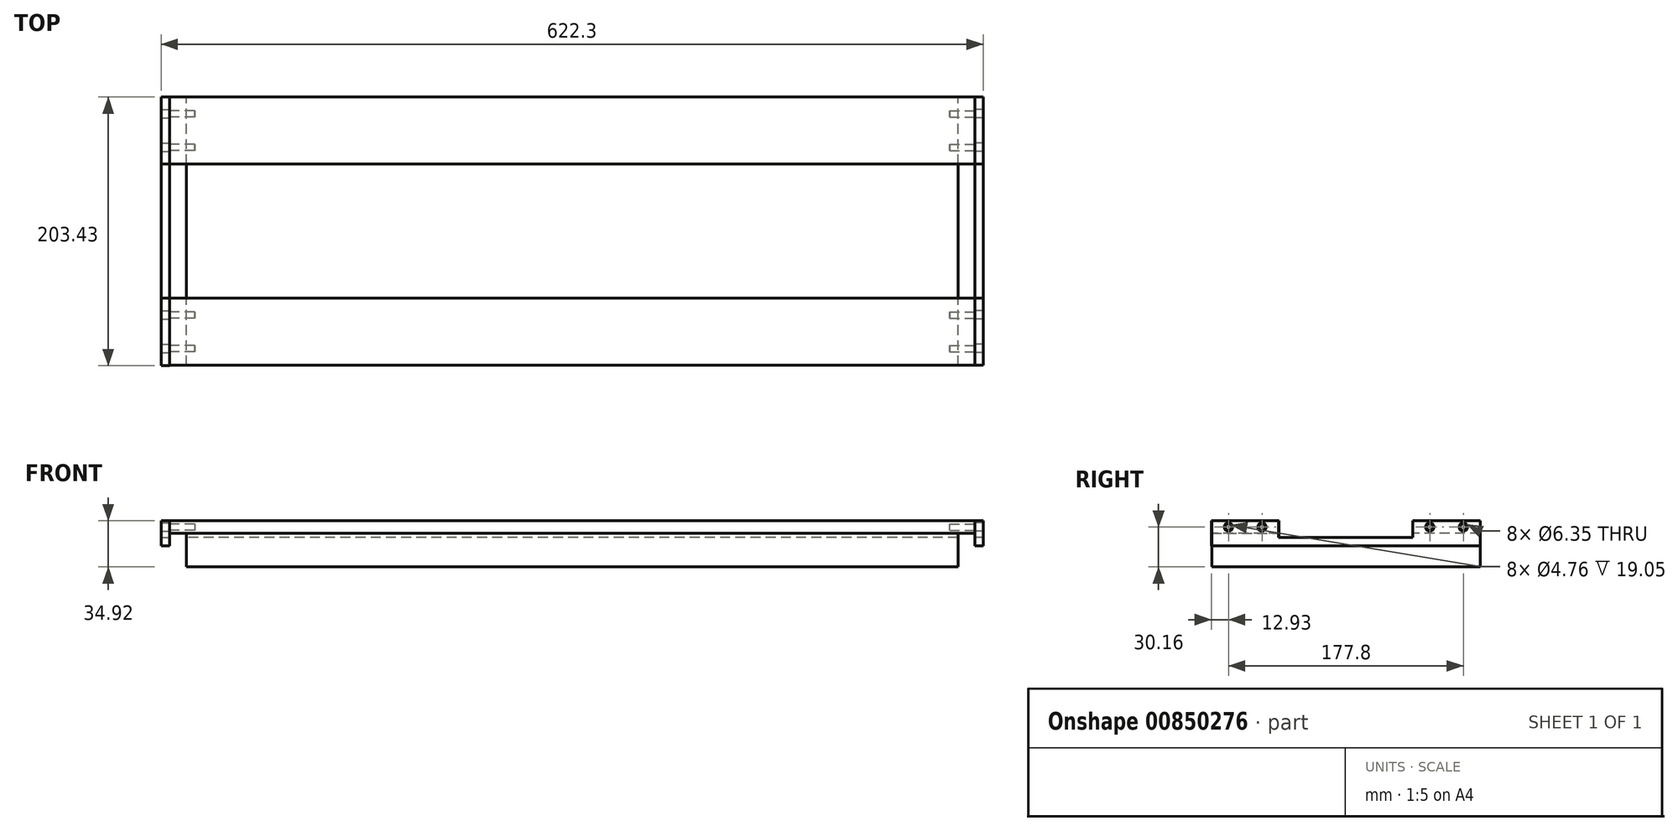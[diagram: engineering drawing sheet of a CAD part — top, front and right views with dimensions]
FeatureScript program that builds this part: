
annotation { "Feature Type Name" : "Feature", "Feature Type Description" : "" }
export const myFeature = defineFeature(function(context is Context, id is Id, definition is map)
    precondition{}
    {
        {
            var Q0;
            Q0=qCreatedBy(makeId("Right.planeOp"),FACE);
            var sketch = newSketch(context, id + "F0", { "sketchPlane" : qUnion([Q0])});
            skLineSegment(sketch, "E0.bottom", {"start": v(-50.8, -4.7) * mm, "end": v(-101.6, -4.7) * mm});
            skLineSegment(sketch, "E0.top", {"start": v(-50.8, 4.7) * mm, "end": v(-101.6, 4.7) * mm});
            skLineSegment(sketch, "E0.left", {"start": v(-50.8, -4.7) * mm, "end": v(-50.8, 4.7) * mm});
            skLineSegment(sketch, "E0.right", {"start": v(-101.6, -4.7) * mm, "end": v(-101.6, 4.7) * mm});
            skPoint(sketch, "E0.middle", {"position": v(-76.2, 0) * mm});
            skLineSegment(sketch, "E1.bottom", {"start": v(101.6, -4.76) * mm, "end": v(50.8, -4.76) * mm});
            skLineSegment(sketch, "E1.top", {"start": v(101.6, 4.76) * mm, "end": v(50.8, 4.76) * mm});
            skLineSegment(sketch, "E1.left", {"start": v(101.6, -4.76) * mm, "end": v(101.6, 4.76) * mm});
            skLineSegment(sketch, "E1.right", {"start": v(50.8, -4.76) * mm, "end": v(50.8, 4.76) * mm});
            skPoint(sketch, "E1.middle", {"position": v(76.2, 0) * mm});
            skSolve(sketch);
        }
        {
            var Q0;
            Q0=makeQuery(id+"F0.imprint","IMPRINT",FACE,{"disambiguationData":[TD([[makeQuery(id+"F0.imprint","IMPRINT",EDGE,{"derivedFrom":sQuery(id+"F0.wireOp",EDGE,"E0.bottom")}),-1.0]])]});
            var Q1;
            Q1=makeQuery(id+"F0.imprint","IMPRINT",FACE,{"disambiguationData":[TD([[makeQuery(id+"F0.imprint","IMPRINT",EDGE,{"derivedFrom":sQuery(id+"F0.wireOp",EDGE,"E1.bottom")}),-1.0]])]});
            extrude(context, id + "F1", {"entities" : qUnion([Q0, Q1]), "endBound" : BoundingType.SYMMETRIC, "depth" : 609.6 * mm, "offsetDistance" : 25.4 * mm});
        }
        {
            var Q0;
            Q0=makeQuery(id+"F1.opExtrude","CAP_FACE",FACE,{"disambiguationData":[OSD([sQuery(id+"F0.wireOp",EDGE,"E0.bottom"),sQuery(id+"F0.wireOp",EDGE,"E0.top"),sQuery(id+"F0.wireOp",EDGE,"E0.left"),sQuery(id+"F0.wireOp",EDGE,"E0.right")])],"isStart":false});
            var sketch = newSketch(context, id + "F2", { "sketchPlane" : qUnion([Q0])});
            skLineSegment(sketch, "E2", {"start": v(-101.6, 0) * mm, "end": v(-50.8, 0) * mm, "construction": true});
            skCircle(sketch, "E3", {"center": v(-88.9, 0) * mm, "radius": 2.38 * mm});
            skCircle(sketch, "E4", {"center": v(-63.5, 0) * mm, "radius": 2.38 * mm});
            skLineSegment(sketch, "E5", {"start": v(-50.8, 0) * mm, "end": v(103.45, 0) * mm, "construction": true});
            skCircle(sketch, "E6", {"center": v(63.5, 0) * mm, "radius": 2.38 * mm});
            skCircle(sketch, "E7", {"center": v(88.9, 0) * mm, "radius": 2.38 * mm});
            skSolve(sketch);
        }
        {
            var Q0;
            Q0 = qSketchRegion(id + "F2", true);
            extrude(context, id + "F3", {"entities" : qUnion([Q0]), "operationType" : NewBodyOperationType.REMOVE, "oppositeDirection" : true, "depth" : 19.05 * mm, "offsetDistance" : 25.4 * mm});
        }
        {
            var Q0;
            Q0=makeQuery(id+"F1.opExtrude","CAP_FACE",FACE,{"disambiguationData":[OSD([sQuery(id+"F0.wireOp",EDGE,"E1.bottom"),sQuery(id+"F0.wireOp",EDGE,"E1.top"),sQuery(id+"F0.wireOp",EDGE,"E1.left"),sQuery(id+"F0.wireOp",EDGE,"E1.right")])],"isStart":true});
            var sketch = newSketch(context, id + "F4", { "sketchPlane" : qUnion([Q0])});
            skLineSegment(sketch, "E8", {"start": v(-101.6, 0) * mm, "end": v(107.91, 0) * mm, "construction": true});
            skCircle(sketch, "E9", {"center": v(-88.9, 0) * mm, "radius": 2.38 * mm});
            skCircle(sketch, "E10", {"center": v(-63.5, 0) * mm, "radius": 2.38 * mm});
            skCircle(sketch, "E11", {"center": v(63.5, 0) * mm, "radius": 2.38 * mm});
            skCircle(sketch, "E12", {"center": v(88.9, 0) * mm, "radius": 2.38 * mm});
            skSolve(sketch);
        }
        {
            var Q0;
            Q0 = qSketchRegion(id + "F4", true);
            extrude(context, id + "F5", {"entities" : qUnion([Q0]), "operationType" : NewBodyOperationType.REMOVE, "oppositeDirection" : true, "depth" : 19.05 * mm, "offsetDistance" : 25.4 * mm});
        }
        {
            var Q0;
            Q0=makeQuery(id+"F1.opExtrude","CAP_FACE",FACE,{"disambiguationData":[OSD([sQuery(id+"F0.wireOp",EDGE,"E1.bottom"),sQuery(id+"F0.wireOp",EDGE,"E1.top"),sQuery(id+"F0.wireOp",EDGE,"E1.left"),sQuery(id+"F0.wireOp",EDGE,"E1.right")])],"isStart":true});
            var sketch = newSketch(context, id + "F6", { "sketchPlane" : qUnion([Q0])});
            skLineSegment(sketch, "E13.bottom", {"start": v(-101.6, 4.76) * mm, "end": v(-50.8, 4.76) * mm});
            skLineSegment(sketch, "E13.top", {"start": v(-101.6, -14.29) * mm, "end": v(101.83, -14.29) * mm});
            skLineSegment(sketch, "E13.left", {"start": v(-101.6, 4.76) * mm, "end": v(-101.6, -14.29) * mm});
            skLineSegment(sketch, "E13.right", {"start": v(101.83, 4.76) * mm, "end": v(101.83, -14.29) * mm});
            skLineSegment(sketch, "E14.top", {"start": v(-50.8, -7.94) * mm, "end": v(50.74, -7.94) * mm});
            skLineSegment(sketch, "E14.left", {"start": v(-50.8, 4.76) * mm, "end": v(-50.8, -7.94) * mm});
            skLineSegment(sketch, "E14.right", {"start": v(50.74, 4.76) * mm, "end": v(50.74, -7.94) * mm});
            skLineSegment(sketch, "E15.trimOffspring", {"start": v(50.74, 4.76) * mm, "end": v(101.83, 4.76) * mm});
            skCircle(sketch, "E16", {"center": v(-88.9, 0) * mm, "radius": 3.18 * mm});
            skCircle(sketch, "E17", {"center": v(-63.5, 0) * mm, "radius": 3.18 * mm});
            skCircle(sketch, "E18", {"center": v(63.5, 0) * mm, "radius": 3.18 * mm});
            skCircle(sketch, "E19", {"center": v(88.9, 0) * mm, "radius": 3.18 * mm});
            skSolve(sketch);
        }
        {
            var Q0;
            {var subQ3=sQuery(id+"F6.wireOp",EDGE,"E13.top");Q0=makeQuery(id+"F6.imprint","IMPRINT",FACE,{"disambiguationData":[TD([[makeQuery(id+"F6.imprint","IMPRINT",EDGE,{"derivedFrom":subQ3}),1.0]])]});}
            var Q1;
            {var subQ2=sQuery(id+"F6.wireOp",EDGE,"E13.bottom");Q1=makeQuery(id+"F6.imprint","IMPRINT",FACE,{"disambiguationData":[TD([[makeQuery(id+"F6.imprint","IMPRINT",EDGE,{"derivedFrom":subQ2}),-1.0]])]});}
            extrude(context, id + "F7", {"entities" : qUnion([Q0, Q1]), "depth" : 6.35 * mm, "offsetDistance" : 25.4 * mm});
        }
        {
            var Q0;
            Q0=makeQuery(id+"F1.opExtrude","CAP_FACE",FACE,{"disambiguationData":[OSD([sQuery(id+"F0.wireOp",EDGE,"E0.bottom"),sQuery(id+"F0.wireOp",EDGE,"E0.top"),sQuery(id+"F0.wireOp",EDGE,"E0.left"),sQuery(id+"F0.wireOp",EDGE,"E0.right")])],"isStart":false});
            var sketch = newSketch(context, id + "F8", { "sketchPlane" : qUnion([Q0])});
            skLineSegment(sketch, "E20.bottom", {"start": v(-101.6, 4.7) * mm, "end": v(-50.8, 4.7) * mm});
            skLineSegment(sketch, "E20.top", {"start": v(-101.6, -14.35) * mm, "end": v(101.6, -14.35) * mm});
            skLineSegment(sketch, "E20.left", {"start": v(-101.6, 4.7) * mm, "end": v(-101.6, -14.35) * mm});
            skLineSegment(sketch, "E20.right", {"start": v(101.6, 4.7) * mm, "end": v(101.6, -14.35) * mm});
            skLineSegment(sketch, "E21.top", {"start": v(-50.8, -8) * mm, "end": v(50.8, -8) * mm});
            skLineSegment(sketch, "E21.left", {"start": v(-50.8, 4.7) * mm, "end": v(-50.8, -8) * mm});
            skLineSegment(sketch, "E21.right", {"start": v(50.8, 4.7) * mm, "end": v(50.8, -8) * mm});
            skLineSegment(sketch, "E22.trimOffspring", {"start": v(50.8, 4.7) * mm, "end": v(101.6, 4.7) * mm});
            skCircle(sketch, "E23", {"center": v(-88.9, 0) * mm, "radius": 3.18 * mm});
            skCircle(sketch, "E24", {"center": v(-63.5, 0) * mm, "radius": 3.18 * mm});
            skCircle(sketch, "E25", {"center": v(63.5, 0) * mm, "radius": 3.18 * mm});
            skCircle(sketch, "E26", {"center": v(88.9, 0) * mm, "radius": 3.18 * mm});
            skSolve(sketch);
        }
        {
            var Q0;
            Q0 = qSketchRegion(id + "F8", true);
            extrude(context, id + "F9", {"entities" : qUnion([Q0]), "depth" : 6.35 * mm, "offsetDistance" : 25.4 * mm});
        }
        {
            var Q0;
            Q0=makeQuery(id+"F7.opExtrude","CAP_FACE",FACE,{"disambiguationData":[OSD([sQuery(id+"F6.wireOp",EDGE,"E13.bottom"),sQuery(id+"F6.wireOp",EDGE,"E13.top"),sQuery(id+"F6.wireOp",EDGE,"E13.left"),sQuery(id+"F6.wireOp",EDGE,"E13.right"),sQuery(id+"F6.wireOp",EDGE,"E14.top"),sQuery(id+"F6.wireOp",EDGE,"E14.left"),sQuery(id+"F6.wireOp",EDGE,"E14.right"),sQuery(id+"F6.wireOp",EDGE,"E15.trimOffspring"),sQuery(id+"F6.wireOp",EDGE,"E16"),sQuery(id+"F6.wireOp",EDGE,"E17"),sQuery(id+"F6.wireOp",EDGE,"E18"),sQuery(id+"F6.wireOp",EDGE,"E19")])],"isStart":true});
            cPlane(context, id + "F10", {"entities" : qUnion([Q0]), "cplaneType" : CPlaneType.OFFSET, "offset" : 12.7 * mm, "width" : 152.4 * mm, "height" : 152.4 * mm});
        }
        {
            var Q0;
            Q0=qCreatedBy(id+"F10.planeOp",FACE);
            var sketch = newSketch(context, id + "F11", { "sketchPlane" : qUnion([Q0])});
            skLineSegment(sketch, "E27.bottom", {"start": v(101.6, -30.16) * mm, "end": v(-101.6, -30.16) * mm});
            skLineSegment(sketch, "E27.left", {"start": v(101.6, -30.16) * mm, "end": v(101.6, -4.76) * mm});
            skLineSegment(sketch, "E27.right", {"start": v(-101.6, -30.16) * mm, "end": v(-101.6, -4.76) * mm});
            skPoint(sketch, "E27.middle", {"position": v(0, 0) * mm});
            skLineSegment(sketch, "E28", {"start": v(-101.6, -4.76) * mm, "end": v(-50.8, -4.76) * mm});
            skPoint(sketch, "E29.orphan", {"position": v(-101.6, 30.16) * mm});
            skPoint(sketch, "E30.orphan", {"position": v(101.6, 30.16) * mm});
            skLineSegment(sketch, "E31.top", {"start": v(50.8, -7.94) * mm, "end": v(-50.8, -7.94) * mm});
            skLineSegment(sketch, "E31.left", {"start": v(50.8, -4.76) * mm, "end": v(50.8, -7.94) * mm});
            skLineSegment(sketch, "E31.right", {"start": v(-50.8, -4.76) * mm, "end": v(-50.8, -7.94) * mm});
            skPoint(sketch, "E31.bottom.end.orphan", {"position": v(-50.8, 7.94) * mm});
            skPoint(sketch, "E31.bottom.start.orphan", {"position": v(50.8, 7.94) * mm});
            skLineSegment(sketch, "E32.trimOffspring", {"start": v(50.8, -4.76) * mm, "end": v(101.6, -4.76) * mm});
            skSolve(sketch);
        }
        {
            var Q0;
            Q0 = qSketchRegion(id + "F11", true);
            extrude(context, id + "F12", {"entities" : qUnion([Q0]), "depth" : 584.2 * mm, "offsetDistance" : 25.4 * mm});
        }
    });
